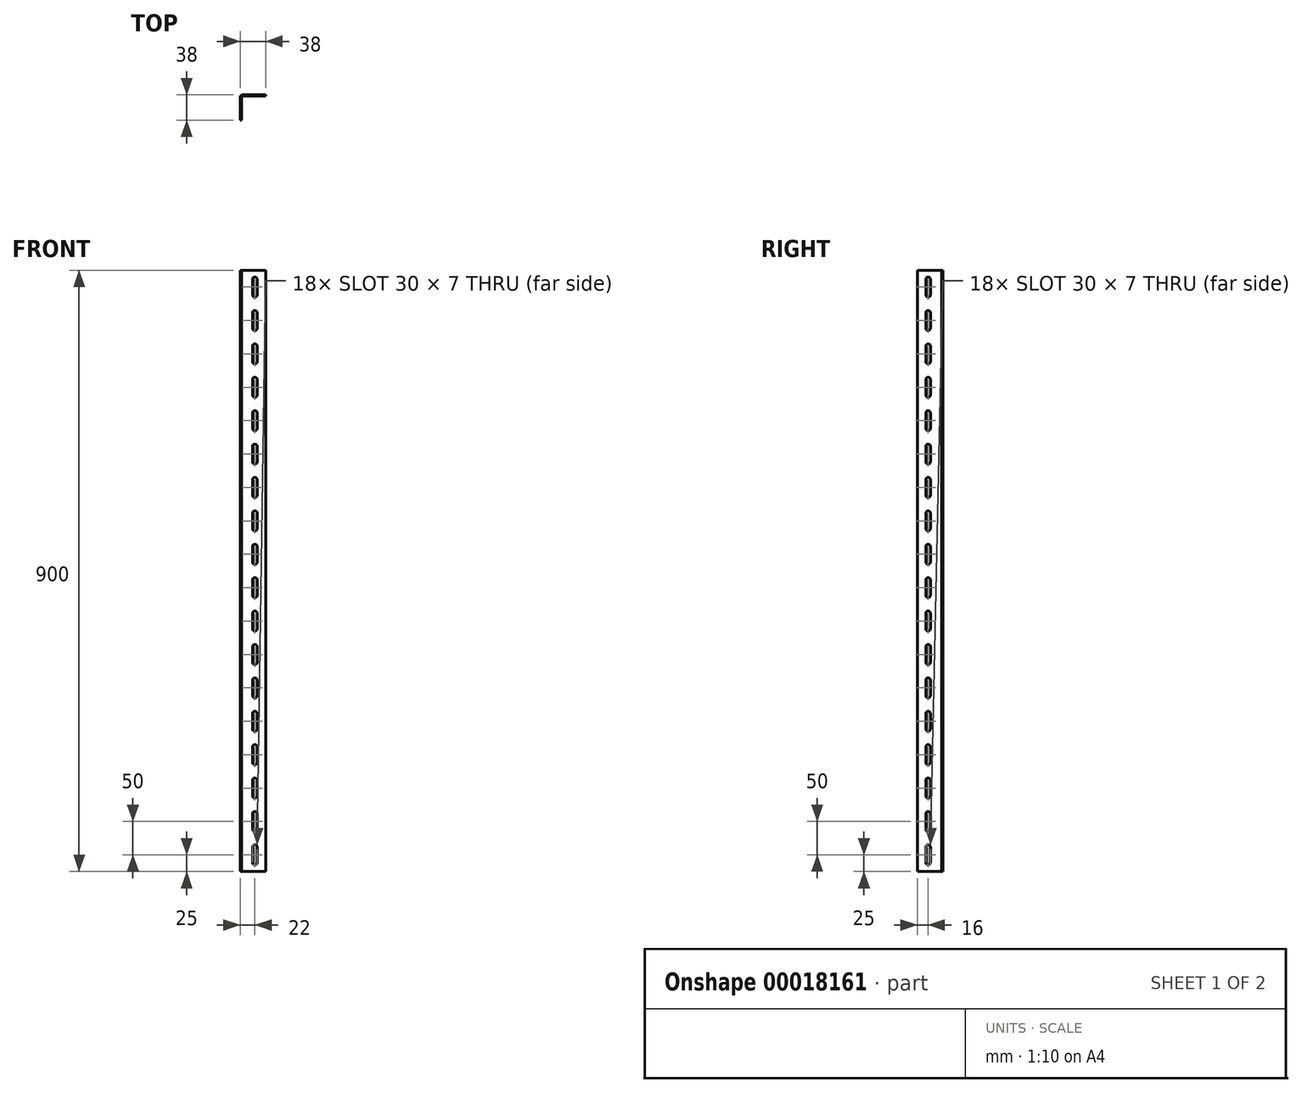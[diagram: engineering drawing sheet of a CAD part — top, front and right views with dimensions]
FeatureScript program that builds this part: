
annotation { "Feature Type Name" : "Feature", "Feature Type Description" : "" }
export const myFeature = defineFeature(function(context is Context, id is Id, definition is map)
    precondition{}
    {
        {
            var Q0;
            Q0=qCreatedBy(makeId("Top.planeOp"),FACE);
            var sketch = newSketch(context, id + "F0", { "sketchPlane" : qUnion([Q0])});
            skLineSegment(sketch, "E0", {"start": v(4.3, 0) * mm, "end": v(38, 0) * mm});
            skLineSegment(sketch, "E1", {"start": v(38, 0) * mm, "end": v(38, -1.8) * mm});
            skLineSegment(sketch, "E2", {"start": v(38, -1.8) * mm, "end": v(4.3, -1.8) * mm});
            skLineSegment(sketch, "E3", {"start": v(1.8, -4.3) * mm, "end": v(1.8, -38) * mm});
            skLineSegment(sketch, "E4", {"start": v(1.8, -38) * mm, "end": v(0, -38) * mm});
            skLineSegment(sketch, "E5", {"start": v(0, -38) * mm, "end": v(0, -4.3) * mm});
            skPoint(sketch, "E6.visualSharp", {"position": v(1.8, -1.8) * mm});
            skArc(sketch, "E6.filletArc", {"start": v(4.3, -1.8) * mm, "mid": v(2.53, -2.53) * mm, "end": v(1.8, -4.3) * mm});
            skPoint(sketch, "E7.visualSharp", {"position": v(0, 0) * mm});
            skArc(sketch, "E7.filletArc", {"start": v(4.3, 0) * mm, "mid": v(1.26, -1.26) * mm, "end": v(0, -4.3) * mm});
            skSolve(sketch);
        }
        {
            var Q0;
            Q0 = qSketchRegion(id + "F0", true);
            extrude(context, id + "F1", {"entities" : qUnion([Q0]), "depth" : 900 * mm});
        }
        {
            var Q0;
            Q0=makeQuery(id+"F1.opExtrude","SWEPT_FACE",FACE,{"disambiguationData":[OSD([sQuery(id+"F0.wireOp",EDGE,"E2")])]});
            var sketch = newSketch(context, id + "F2", { "sketchPlane" : qUnion([Q0])});
            skLineSegment(sketch, "E8", {"start": v(22, 900) * mm, "end": v(22, 701.08) * mm, "construction": true});
            skArc(sketch, "E9", {"start": v(25.5, 886.5) * mm, "mid": v(22, 890) * mm, "end": v(18.5, 886.5) * mm});
            skArc(sketch, "E10", {"start": v(18.5, 863.5) * mm, "mid": v(22, 860) * mm, "end": v(25.5, 863.5) * mm});
            skLineSegment(sketch, "E11", {"start": v(18.5, 886.5) * mm, "end": v(18.5, 863.5) * mm});
            skLineSegment(sketch, "E12", {"start": v(25.5, 863.5) * mm, "end": v(25.5, 886.5) * mm});
            skArc(sketch, "E13.0.1.0", {"start": v(25.5, 836.5) * mm, "mid": v(22, 840) * mm, "end": v(18.5, 836.5) * mm});
            skLineSegment(sketch, "E13.0.1.1", {"start": v(18.5, 836.5) * mm, "end": v(18.5, 813.5) * mm});
            skLineSegment(sketch, "E13.0.1.2", {"start": v(25.5, 813.5) * mm, "end": v(25.5, 836.5) * mm});
            skArc(sketch, "E13.0.1.3", {"start": v(18.5, 813.5) * mm, "mid": v(22, 810) * mm, "end": v(25.5, 813.5) * mm});
            skArc(sketch, "E13.0.2.0", {"start": v(25.5, 786.5) * mm, "mid": v(22, 790) * mm, "end": v(18.5, 786.5) * mm});
            skLineSegment(sketch, "E13.0.2.1", {"start": v(18.5, 786.5) * mm, "end": v(18.5, 763.5) * mm});
            skLineSegment(sketch, "E13.0.2.2", {"start": v(25.5, 763.5) * mm, "end": v(25.5, 786.5) * mm});
            skArc(sketch, "E13.0.2.3", {"start": v(18.5, 763.5) * mm, "mid": v(22, 760) * mm, "end": v(25.5, 763.5) * mm});
            skArc(sketch, "E13.0.3.0", {"start": v(25.5, 736.5) * mm, "mid": v(22, 740) * mm, "end": v(18.5, 736.5) * mm});
            skLineSegment(sketch, "E13.0.3.1", {"start": v(18.5, 736.5) * mm, "end": v(18.5, 713.5) * mm});
            skLineSegment(sketch, "E13.0.3.2", {"start": v(25.5, 713.5) * mm, "end": v(25.5, 736.5) * mm});
            skArc(sketch, "E13.0.3.3", {"start": v(18.5, 713.5) * mm, "mid": v(22, 710) * mm, "end": v(25.5, 713.5) * mm});
            skArc(sketch, "E13.0.4.0", {"start": v(25.5, 686.5) * mm, "mid": v(22, 690) * mm, "end": v(18.5, 686.5) * mm});
            skLineSegment(sketch, "E13.0.4.1", {"start": v(18.5, 686.5) * mm, "end": v(18.5, 663.5) * mm});
            skLineSegment(sketch, "E13.0.4.2", {"start": v(25.5, 663.5) * mm, "end": v(25.5, 686.5) * mm});
            skArc(sketch, "E13.0.4.3", {"start": v(18.5, 663.5) * mm, "mid": v(22, 660) * mm, "end": v(25.5, 663.5) * mm});
            skArc(sketch, "E13.0.5.0", {"start": v(25.5, 636.5) * mm, "mid": v(22, 640) * mm, "end": v(18.5, 636.5) * mm});
            skLineSegment(sketch, "E13.0.5.1", {"start": v(18.5, 636.5) * mm, "end": v(18.5, 613.5) * mm});
            skLineSegment(sketch, "E13.0.5.2", {"start": v(25.5, 613.5) * mm, "end": v(25.5, 636.5) * mm});
            skArc(sketch, "E13.0.5.3", {"start": v(18.5, 613.5) * mm, "mid": v(22, 610) * mm, "end": v(25.5, 613.5) * mm});
            skArc(sketch, "E13.0.6.0", {"start": v(25.5, 586.5) * mm, "mid": v(22, 590) * mm, "end": v(18.5, 586.5) * mm});
            skLineSegment(sketch, "E13.0.6.1", {"start": v(18.5, 586.5) * mm, "end": v(18.5, 563.5) * mm});
            skLineSegment(sketch, "E13.0.6.2", {"start": v(25.5, 563.5) * mm, "end": v(25.5, 586.5) * mm});
            skArc(sketch, "E13.0.6.3", {"start": v(18.5, 563.5) * mm, "mid": v(22, 560) * mm, "end": v(25.5, 563.5) * mm});
            skArc(sketch, "E13.0.7.0", {"start": v(25.5, 536.5) * mm, "mid": v(22, 540) * mm, "end": v(18.5, 536.5) * mm});
            skLineSegment(sketch, "E13.0.7.1", {"start": v(18.5, 536.5) * mm, "end": v(18.5, 513.5) * mm});
            skLineSegment(sketch, "E13.0.7.2", {"start": v(25.5, 513.5) * mm, "end": v(25.5, 536.5) * mm});
            skArc(sketch, "E13.0.7.3", {"start": v(18.5, 513.5) * mm, "mid": v(22, 510) * mm, "end": v(25.5, 513.5) * mm});
            skArc(sketch, "E13.0.8.0", {"start": v(25.5, 486.5) * mm, "mid": v(22, 490) * mm, "end": v(18.5, 486.5) * mm});
            skLineSegment(sketch, "E13.0.8.1", {"start": v(18.5, 486.5) * mm, "end": v(18.5, 463.5) * mm});
            skLineSegment(sketch, "E13.0.8.2", {"start": v(25.5, 463.5) * mm, "end": v(25.5, 486.5) * mm});
            skArc(sketch, "E13.0.8.3", {"start": v(18.5, 463.5) * mm, "mid": v(22, 460) * mm, "end": v(25.5, 463.5) * mm});
            skArc(sketch, "E13.0.9.0", {"start": v(25.5, 436.5) * mm, "mid": v(22, 440) * mm, "end": v(18.5, 436.5) * mm});
            skLineSegment(sketch, "E13.0.9.1", {"start": v(18.5, 436.5) * mm, "end": v(18.5, 413.5) * mm});
            skLineSegment(sketch, "E13.0.9.2", {"start": v(25.5, 413.5) * mm, "end": v(25.5, 436.5) * mm});
            skArc(sketch, "E13.0.9.3", {"start": v(18.5, 413.5) * mm, "mid": v(22, 410) * mm, "end": v(25.5, 413.5) * mm});
            skArc(sketch, "E13.0.10.0", {"start": v(25.5, 386.5) * mm, "mid": v(22, 390) * mm, "end": v(18.5, 386.5) * mm});
            skLineSegment(sketch, "E13.0.10.1", {"start": v(18.5, 386.5) * mm, "end": v(18.5, 363.5) * mm});
            skLineSegment(sketch, "E13.0.10.2", {"start": v(25.5, 363.5) * mm, "end": v(25.5, 386.5) * mm});
            skArc(sketch, "E13.0.10.3", {"start": v(18.5, 363.5) * mm, "mid": v(22, 360) * mm, "end": v(25.5, 363.5) * mm});
            skArc(sketch, "E13.0.11.0", {"start": v(25.5, 336.5) * mm, "mid": v(22, 340) * mm, "end": v(18.5, 336.5) * mm});
            skLineSegment(sketch, "E13.0.11.1", {"start": v(18.5, 336.5) * mm, "end": v(18.5, 313.5) * mm});
            skLineSegment(sketch, "E13.0.11.2", {"start": v(25.5, 313.5) * mm, "end": v(25.5, 336.5) * mm});
            skArc(sketch, "E13.0.11.3", {"start": v(18.5, 313.5) * mm, "mid": v(22, 310) * mm, "end": v(25.5, 313.5) * mm});
            skArc(sketch, "E13.0.12.0", {"start": v(25.5, 286.5) * mm, "mid": v(22, 290) * mm, "end": v(18.5, 286.5) * mm});
            skLineSegment(sketch, "E13.0.12.1", {"start": v(18.5, 286.5) * mm, "end": v(18.5, 263.5) * mm});
            skLineSegment(sketch, "E13.0.12.2", {"start": v(25.5, 263.5) * mm, "end": v(25.5, 286.5) * mm});
            skArc(sketch, "E13.0.12.3", {"start": v(18.5, 263.5) * mm, "mid": v(22, 260) * mm, "end": v(25.5, 263.5) * mm});
            skArc(sketch, "E13.0.13.0", {"start": v(25.5, 236.5) * mm, "mid": v(22, 240) * mm, "end": v(18.5, 236.5) * mm});
            skLineSegment(sketch, "E13.0.13.1", {"start": v(18.5, 236.5) * mm, "end": v(18.5, 213.5) * mm});
            skLineSegment(sketch, "E13.0.13.2", {"start": v(25.5, 213.5) * mm, "end": v(25.5, 236.5) * mm});
            skArc(sketch, "E13.0.13.3", {"start": v(18.5, 213.5) * mm, "mid": v(22, 210) * mm, "end": v(25.5, 213.5) * mm});
            skArc(sketch, "E13.0.14.0", {"start": v(25.5, 186.5) * mm, "mid": v(22, 190) * mm, "end": v(18.5, 186.5) * mm});
            skLineSegment(sketch, "E13.0.14.1", {"start": v(18.5, 186.5) * mm, "end": v(18.5, 163.5) * mm});
            skLineSegment(sketch, "E13.0.14.2", {"start": v(25.5, 163.5) * mm, "end": v(25.5, 186.5) * mm});
            skArc(sketch, "E13.0.14.3", {"start": v(18.5, 163.5) * mm, "mid": v(22, 160) * mm, "end": v(25.5, 163.5) * mm});
            skArc(sketch, "E13.0.15.0", {"start": v(25.5, 136.5) * mm, "mid": v(22, 140) * mm, "end": v(18.5, 136.5) * mm});
            skLineSegment(sketch, "E13.0.15.1", {"start": v(18.5, 136.5) * mm, "end": v(18.5, 113.5) * mm});
            skLineSegment(sketch, "E13.0.15.2", {"start": v(25.5, 113.5) * mm, "end": v(25.5, 136.5) * mm});
            skArc(sketch, "E13.0.15.3", {"start": v(18.5, 113.5) * mm, "mid": v(22, 110) * mm, "end": v(25.5, 113.5) * mm});
            skArc(sketch, "E13.0.16.0", {"start": v(25.5, 86.5) * mm, "mid": v(22, 90) * mm, "end": v(18.5, 86.5) * mm});
            skLineSegment(sketch, "E13.0.16.1", {"start": v(18.5, 86.5) * mm, "end": v(18.5, 63.5) * mm});
            skLineSegment(sketch, "E13.0.16.2", {"start": v(25.5, 63.5) * mm, "end": v(25.5, 86.5) * mm});
            skArc(sketch, "E13.0.16.3", {"start": v(18.5, 63.5) * mm, "mid": v(22, 60) * mm, "end": v(25.5, 63.5) * mm});
            skArc(sketch, "E13.0.17.0", {"start": v(25.5, 36.5) * mm, "mid": v(22, 40) * mm, "end": v(18.5, 36.5) * mm});
            skLineSegment(sketch, "E13.0.17.1", {"start": v(18.5, 36.5) * mm, "end": v(18.5, 13.5) * mm});
            skLineSegment(sketch, "E13.0.17.2", {"start": v(25.5, 13.5) * mm, "end": v(25.5, 36.5) * mm});
            skArc(sketch, "E13.0.17.3", {"start": v(18.5, 13.5) * mm, "mid": v(22, 10) * mm, "end": v(25.5, 13.5) * mm});
            skLineSegment(sketch, "E13.direction1", {"start": v(18.5, 886.5) * mm, "end": v(43.9, 886.5) * mm, "construction": true});
            skLineSegment(sketch, "E13.direction2", {"start": v(18.5, 886.5) * mm, "end": v(18.5, 836.5) * mm, "construction": true});
            skSolve(sketch);
        }
        {
            var Q0;
            Q0 = qSketchRegion(id + "F2", true);
            extrude(context, id + "F3", {"entities" : qUnion([Q0]), "operationType" : NewBodyOperationType.REMOVE, "endBound" : BoundingType.UP_TO_NEXT, "oppositeDirection" : true, "depth" : 25.4 * mm});
        }
        {
            var Q0;
            Q0=makeQuery(id+"F1.opExtrude","SWEPT_FACE",FACE,{"disambiguationData":[OSD([sQuery(id+"F0.wireOp",EDGE,"E3")])]});
            var sketch = newSketch(context, id + "F4", { "sketchPlane" : qUnion([Q0])});
            skLineSegment(sketch, "E14", {"start": v(-22, 884.02) * mm, "end": v(-22, 685.1) * mm, "construction": true});
            skArc(sketch, "E15", {"start": v(-18.5, 886.5) * mm, "mid": v(-22, 890) * mm, "end": v(-25.5, 886.5) * mm});
            skArc(sketch, "E16", {"start": v(-25.5, 863.5) * mm, "mid": v(-22, 860) * mm, "end": v(-18.5, 863.5) * mm});
            skLineSegment(sketch, "E17", {"start": v(-25.5, 886.5) * mm, "end": v(-25.5, 863.5) * mm});
            skLineSegment(sketch, "E18", {"start": v(-18.5, 863.5) * mm, "end": v(-18.5, 886.5) * mm});
            skArc(sketch, "E19.0.1.0", {"start": v(-18.5, 836.5) * mm, "mid": v(-22, 840) * mm, "end": v(-25.5, 836.5) * mm});
            skLineSegment(sketch, "E19.0.1.1", {"start": v(-25.5, 836.5) * mm, "end": v(-25.5, 813.5) * mm});
            skLineSegment(sketch, "E19.0.1.2", {"start": v(-18.5, 813.5) * mm, "end": v(-18.5, 836.5) * mm});
            skArc(sketch, "E19.0.1.3", {"start": v(-25.5, 813.5) * mm, "mid": v(-22, 810) * mm, "end": v(-18.5, 813.5) * mm});
            skArc(sketch, "E19.0.2.0", {"start": v(-18.5, 786.5) * mm, "mid": v(-22, 790) * mm, "end": v(-25.5, 786.5) * mm});
            skLineSegment(sketch, "E19.0.2.1", {"start": v(-25.5, 786.5) * mm, "end": v(-25.5, 763.5) * mm});
            skLineSegment(sketch, "E19.0.2.2", {"start": v(-18.5, 763.5) * mm, "end": v(-18.5, 786.5) * mm});
            skArc(sketch, "E19.0.2.3", {"start": v(-25.5, 763.5) * mm, "mid": v(-22, 760) * mm, "end": v(-18.5, 763.5) * mm});
            skArc(sketch, "E19.0.3.0", {"start": v(-18.5, 736.5) * mm, "mid": v(-22, 740) * mm, "end": v(-25.5, 736.5) * mm});
            skLineSegment(sketch, "E19.0.3.1", {"start": v(-25.5, 736.5) * mm, "end": v(-25.5, 713.5) * mm});
            skLineSegment(sketch, "E19.0.3.2", {"start": v(-18.5, 713.5) * mm, "end": v(-18.5, 736.5) * mm});
            skArc(sketch, "E19.0.3.3", {"start": v(-25.5, 713.5) * mm, "mid": v(-22, 710) * mm, "end": v(-18.5, 713.5) * mm});
            skArc(sketch, "E19.0.4.0", {"start": v(-18.5, 686.5) * mm, "mid": v(-22, 690) * mm, "end": v(-25.5, 686.5) * mm});
            skLineSegment(sketch, "E19.0.4.1", {"start": v(-25.5, 686.5) * mm, "end": v(-25.5, 663.5) * mm});
            skLineSegment(sketch, "E19.0.4.2", {"start": v(-18.5, 663.5) * mm, "end": v(-18.5, 686.5) * mm});
            skArc(sketch, "E19.0.4.3", {"start": v(-25.5, 663.5) * mm, "mid": v(-22, 660) * mm, "end": v(-18.5, 663.5) * mm});
            skArc(sketch, "E19.0.5.0", {"start": v(-18.5, 636.5) * mm, "mid": v(-22, 640) * mm, "end": v(-25.5, 636.5) * mm});
            skLineSegment(sketch, "E19.0.5.1", {"start": v(-25.5, 636.5) * mm, "end": v(-25.5, 613.5) * mm});
            skLineSegment(sketch, "E19.0.5.2", {"start": v(-18.5, 613.5) * mm, "end": v(-18.5, 636.5) * mm});
            skArc(sketch, "E19.0.5.3", {"start": v(-25.5, 613.5) * mm, "mid": v(-22, 610) * mm, "end": v(-18.5, 613.5) * mm});
            skArc(sketch, "E19.0.6.0", {"start": v(-18.5, 586.5) * mm, "mid": v(-22, 590) * mm, "end": v(-25.5, 586.5) * mm});
            skLineSegment(sketch, "E19.0.6.1", {"start": v(-25.5, 586.5) * mm, "end": v(-25.5, 563.5) * mm});
            skLineSegment(sketch, "E19.0.6.2", {"start": v(-18.5, 563.5) * mm, "end": v(-18.5, 586.5) * mm});
            skArc(sketch, "E19.0.6.3", {"start": v(-25.5, 563.5) * mm, "mid": v(-22, 560) * mm, "end": v(-18.5, 563.5) * mm});
            skArc(sketch, "E19.0.7.0", {"start": v(-18.5, 536.5) * mm, "mid": v(-22, 540) * mm, "end": v(-25.5, 536.5) * mm});
            skLineSegment(sketch, "E19.0.7.1", {"start": v(-25.5, 536.5) * mm, "end": v(-25.5, 513.5) * mm});
            skLineSegment(sketch, "E19.0.7.2", {"start": v(-18.5, 513.5) * mm, "end": v(-18.5, 536.5) * mm});
            skArc(sketch, "E19.0.7.3", {"start": v(-25.5, 513.5) * mm, "mid": v(-22, 510) * mm, "end": v(-18.5, 513.5) * mm});
            skArc(sketch, "E19.0.8.0", {"start": v(-18.5, 486.5) * mm, "mid": v(-22, 490) * mm, "end": v(-25.5, 486.5) * mm});
            skLineSegment(sketch, "E19.0.8.1", {"start": v(-25.5, 486.5) * mm, "end": v(-25.5, 463.5) * mm});
            skLineSegment(sketch, "E19.0.8.2", {"start": v(-18.5, 463.5) * mm, "end": v(-18.5, 486.5) * mm});
            skArc(sketch, "E19.0.8.3", {"start": v(-25.5, 463.5) * mm, "mid": v(-22, 460) * mm, "end": v(-18.5, 463.5) * mm});
            skArc(sketch, "E19.0.9.0", {"start": v(-18.5, 436.5) * mm, "mid": v(-22, 440) * mm, "end": v(-25.5, 436.5) * mm});
            skLineSegment(sketch, "E19.0.9.1", {"start": v(-25.5, 436.5) * mm, "end": v(-25.5, 413.5) * mm});
            skLineSegment(sketch, "E19.0.9.2", {"start": v(-18.5, 413.5) * mm, "end": v(-18.5, 436.5) * mm});
            skArc(sketch, "E19.0.9.3", {"start": v(-25.5, 413.5) * mm, "mid": v(-22, 410) * mm, "end": v(-18.5, 413.5) * mm});
            skArc(sketch, "E19.0.10.0", {"start": v(-18.5, 386.5) * mm, "mid": v(-22, 390) * mm, "end": v(-25.5, 386.5) * mm});
            skLineSegment(sketch, "E19.0.10.1", {"start": v(-25.5, 386.5) * mm, "end": v(-25.5, 363.5) * mm});
            skLineSegment(sketch, "E19.0.10.2", {"start": v(-18.5, 363.5) * mm, "end": v(-18.5, 386.5) * mm});
            skArc(sketch, "E19.0.10.3", {"start": v(-25.5, 363.5) * mm, "mid": v(-22, 360) * mm, "end": v(-18.5, 363.5) * mm});
            skArc(sketch, "E19.0.11.0", {"start": v(-18.5, 336.5) * mm, "mid": v(-22, 340) * mm, "end": v(-25.5, 336.5) * mm});
            skLineSegment(sketch, "E19.0.11.1", {"start": v(-25.5, 336.5) * mm, "end": v(-25.5, 313.5) * mm});
            skLineSegment(sketch, "E19.0.11.2", {"start": v(-18.5, 313.5) * mm, "end": v(-18.5, 336.5) * mm});
            skArc(sketch, "E19.0.11.3", {"start": v(-25.5, 313.5) * mm, "mid": v(-22, 310) * mm, "end": v(-18.5, 313.5) * mm});
            skArc(sketch, "E19.0.12.0", {"start": v(-18.5, 286.5) * mm, "mid": v(-22, 290) * mm, "end": v(-25.5, 286.5) * mm});
            skLineSegment(sketch, "E19.0.12.1", {"start": v(-25.5, 286.5) * mm, "end": v(-25.5, 263.5) * mm});
            skLineSegment(sketch, "E19.0.12.2", {"start": v(-18.5, 263.5) * mm, "end": v(-18.5, 286.5) * mm});
            skArc(sketch, "E19.0.12.3", {"start": v(-25.5, 263.5) * mm, "mid": v(-22, 260) * mm, "end": v(-18.5, 263.5) * mm});
            skArc(sketch, "E19.0.13.0", {"start": v(-18.5, 236.5) * mm, "mid": v(-22, 240) * mm, "end": v(-25.5, 236.5) * mm});
            skLineSegment(sketch, "E19.0.13.1", {"start": v(-25.5, 236.5) * mm, "end": v(-25.5, 213.5) * mm});
            skLineSegment(sketch, "E19.0.13.2", {"start": v(-18.5, 213.5) * mm, "end": v(-18.5, 236.5) * mm});
            skArc(sketch, "E19.0.13.3", {"start": v(-25.5, 213.5) * mm, "mid": v(-22, 210) * mm, "end": v(-18.5, 213.5) * mm});
            skArc(sketch, "E19.0.14.0", {"start": v(-18.5, 186.5) * mm, "mid": v(-22, 190) * mm, "end": v(-25.5, 186.5) * mm});
            skLineSegment(sketch, "E19.0.14.1", {"start": v(-25.5, 186.5) * mm, "end": v(-25.5, 163.5) * mm});
            skLineSegment(sketch, "E19.0.14.2", {"start": v(-18.5, 163.5) * mm, "end": v(-18.5, 186.5) * mm});
            skArc(sketch, "E19.0.14.3", {"start": v(-25.5, 163.5) * mm, "mid": v(-22, 160) * mm, "end": v(-18.5, 163.5) * mm});
            skArc(sketch, "E19.0.15.0", {"start": v(-18.5, 136.5) * mm, "mid": v(-22, 140) * mm, "end": v(-25.5, 136.5) * mm});
            skLineSegment(sketch, "E19.0.15.1", {"start": v(-25.5, 136.5) * mm, "end": v(-25.5, 113.5) * mm});
            skLineSegment(sketch, "E19.0.15.2", {"start": v(-18.5, 113.5) * mm, "end": v(-18.5, 136.5) * mm});
            skArc(sketch, "E19.0.15.3", {"start": v(-25.5, 113.5) * mm, "mid": v(-22, 110) * mm, "end": v(-18.5, 113.5) * mm});
            skArc(sketch, "E19.0.16.0", {"start": v(-18.5, 86.5) * mm, "mid": v(-22, 90) * mm, "end": v(-25.5, 86.5) * mm});
            skLineSegment(sketch, "E19.0.16.1", {"start": v(-25.5, 86.5) * mm, "end": v(-25.5, 63.5) * mm});
            skLineSegment(sketch, "E19.0.16.2", {"start": v(-18.5, 63.5) * mm, "end": v(-18.5, 86.5) * mm});
            skArc(sketch, "E19.0.16.3", {"start": v(-25.5, 63.5) * mm, "mid": v(-22, 60) * mm, "end": v(-18.5, 63.5) * mm});
            skArc(sketch, "E19.0.17.0", {"start": v(-18.5, 36.5) * mm, "mid": v(-22, 40) * mm, "end": v(-25.5, 36.5) * mm});
            skLineSegment(sketch, "E19.0.17.1", {"start": v(-25.5, 36.5) * mm, "end": v(-25.5, 13.5) * mm});
            skLineSegment(sketch, "E19.0.17.2", {"start": v(-18.5, 13.5) * mm, "end": v(-18.5, 36.5) * mm});
            skArc(sketch, "E19.0.17.3", {"start": v(-25.5, 13.5) * mm, "mid": v(-22, 10) * mm, "end": v(-18.5, 13.5) * mm});
            skLineSegment(sketch, "E19.direction1", {"start": v(-25.5, 886.5) * mm, "end": v(0.22, 886.5) * mm, "construction": true});
            skLineSegment(sketch, "E19.direction2", {"start": v(-25.5, 886.5) * mm, "end": v(-25.5, 836.5) * mm, "construction": true});
            skSolve(sketch);
        }
        {
            var Q0;
            Q0 = qSketchRegion(id + "F4", true);
            extrude(context, id + "F5", {"entities" : qUnion([Q0]), "operationType" : NewBodyOperationType.REMOVE, "endBound" : BoundingType.UP_TO_NEXT, "oppositeDirection" : true, "depth" : 25.4 * mm});
        }
    });
